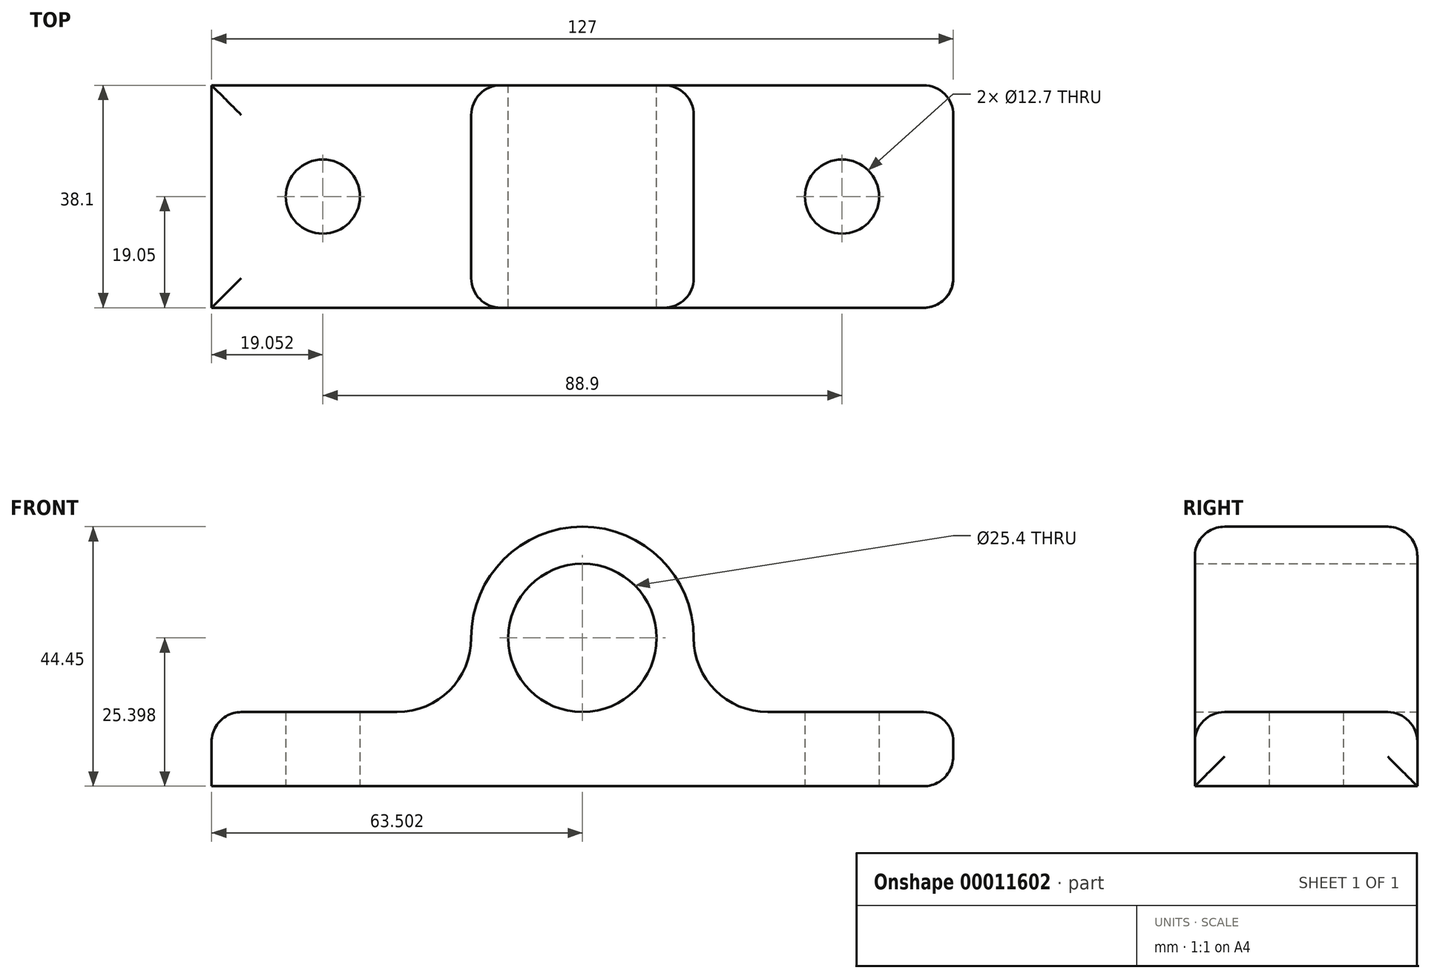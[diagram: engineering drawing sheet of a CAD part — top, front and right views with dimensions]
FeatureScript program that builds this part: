
annotation { "Feature Type Name" : "Feature", "Feature Type Description" : "" }
export const myFeature = defineFeature(function(context is Context, id is Id, definition is map)
    precondition{}
    {
        {
            var Q0;
            Q0=qCreatedBy(makeId("Front.planeOp"),FACE);
            var sketch = newSketch(context, id + "F0", { "sketchPlane" : qUnion([Q0])});
            skLineSegment(sketch, "E0.bottom", {"start": v(-60.1, 16.67) * mm, "end": v(-28.36, 16.67) * mm});
            skLineSegment(sketch, "E0.top", {"start": v(-60.1, 3.97) * mm, "end": v(66.9, 3.97) * mm});
            skLineSegment(sketch, "E0.left", {"start": v(-60.1, 16.67) * mm, "end": v(-60.1, 3.97) * mm});
            skLineSegment(sketch, "E0.right", {"start": v(66.9, 16.67) * mm, "end": v(66.9, 3.97) * mm});
            skLineSegment(sketch, "E1", {"start": v(3.4, 3.97) * mm, "end": v(3.4, 71.82) * mm, "construction": true});
            skLineSegment(sketch, "E2.0", {"start": v(-60.1, 16.67) * mm, "end": v(-28.36, 16.67) * mm, "construction": true});
            skLineSegment(sketch, "E3.0", {"start": v(-60.1, 29.37) * mm, "end": v(66.9, 29.37) * mm, "construction": true});
            skCircle(sketch, "E4", {"center": v(3.4, 29.37) * mm, "radius": 12.7 * mm});
            skArc(sketch, "E5.0", {"start": v(17.6, 16.67) * mm, "mid": v(-10.8, 42.07) * mm, "end": v(17.6, 16.67) * mm});
            skLineSegment(sketch, "E6", {"start": v(-15.66, 29.37) * mm, "end": v(-28.36, 29.37) * mm});
            skArc(sketch, "E7", {"start": v(-28.36, 16.67) * mm, "mid": v(-19.38, 20.39) * mm, "end": v(-15.66, 29.37) * mm});
            skLineSegment(sketch, "E8.trimOffspring", {"start": v(35.14, 16.67) * mm, "end": v(66.9, 16.67) * mm});
            skArc(sketch, "E9.trimOffspring", {"start": v(22.44, 29.37) * mm, "mid": v(3.4, 48.42) * mm, "end": v(-15.66, 29.37) * mm});
            skArc(sketch, "E10.0.MirrorCS", {"start": v(35.14, 16.67) * mm, "mid": v(26.16, 20.39) * mm, "end": v(22.44, 29.37) * mm});
            skLineSegment(sketch, "E11.trimOffspring", {"start": v(35.14, 16.67) * mm, "end": v(66.9, 16.67) * mm, "construction": true});
            skSolve(sketch);
        }
        {
            var Q0;
            Q0=makeQuery(id+"F0.imprint","IMPRINT",FACE,{"disambiguationData":[TD([[makeQuery(id+"F0.imprint","IMPRINT",EDGE,{"derivedFrom":sQuery(id+"F0.wireOp",EDGE,"E0.bottom")}),-1.0]])]});
            extrude(context, id + "F1", {"entities" : qUnion([Q0]), "depth" : 38.1 * mm});
        }
        {
            var Q0;
            Q0=makeQuery(id+"F1.opExtrude","SWEPT_FACE",FACE,{"disambiguationData":[OSD([sQuery(id+"F0.wireOp",EDGE,"E0.top")])]});
            var sketch = newSketch(context, id + "F2", { "sketchPlane" : qUnion([Q0])});
            skLineSegment(sketch, "E12.0", {"start": v(-41.06, 38.1) * mm, "end": v(-41.06, 0) * mm});
            skCircle(sketch, "E13", {"center": v(-41.06, 19.05) * mm, "radius": 6.35 * mm});
            skLineSegment(sketch, "E14", {"start": v(3.4, 0) * mm, "end": v(3.4, 38.1) * mm, "construction": true});
            skCircle(sketch, "E15.0.MirrorC", {"center": v(47.84, 19.05) * mm, "radius": 6.35 * mm});
            skSolve(sketch);
        }
        {
            var Q0;
            Q0 = qSketchRegion(id + "F2", true);
            extrude(context, id + "F3", {"entities" : qUnion([Q0]), "operationType" : NewBodyOperationType.REMOVE, "endBound" : BoundingType.THROUGH_ALL, "oppositeDirection" : true, "depth" : 25.4 * mm});
        }
        {
            var Q0;
            Q0=makeQuery(id+"F1.opExtrude","CAP_EDGE",EDGE,{"disambiguationData":[OSD([sQuery(id+"F0.wireOp",EDGE,"E7")])],"isStart":false});
            var Q1;
            Q1=makeQuery(id+"F3.boolean.opBoolean","COPY",EDGE,{"derivedFrom":makeQuery(id+"F3.opExtrude","CAP_EDGE",EDGE,{"disambiguationData":[OSD([sQuery(id+"F2.wireOp",EDGE,"E13")])],"isStart":true})});
            var Q2;
            Q2=makeQuery(id+"F1.opExtrude","CAP_EDGE",EDGE,{"disambiguationData":[OSD([sQuery(id+"F0.wireOp",EDGE,"E0.bottom")])],"isStart":false});
            var Q3;
            Q3=makeQuery(id+"F1.opExtrude","CAP_EDGE",EDGE,{"disambiguationData":[OSD([sQuery(id+"F0.wireOp",EDGE,"E8.trimOffspring")])],"isStart":true});
            var Q4;
            Q4=makeQuery(id+"F1.opExtrude","SWEPT_FACE",FACE,{"disambiguationData":[OSD([sQuery(id+"F0.wireOp",EDGE,"E0.right")])]});
            var Q5;
            Q5=makeQuery(id+"F1.opExtrude","SWEPT_EDGE",EDGE,{"disambiguationData":[OSD([sQuery(id+"F0.wireOp",EDGE,"E0.bottom"),sQuery(id+"F0.wireOp",EDGE,"E0.left")])]});
            fillet(context, id + "F4", {"entities" : qUnion([Q0, Q1, Q2, Q3, Q4, Q5]), "radius" : 5.08 * mm, "tangentPropagation" : true, "allowEdgeOverflow" : false});
        }
    });
